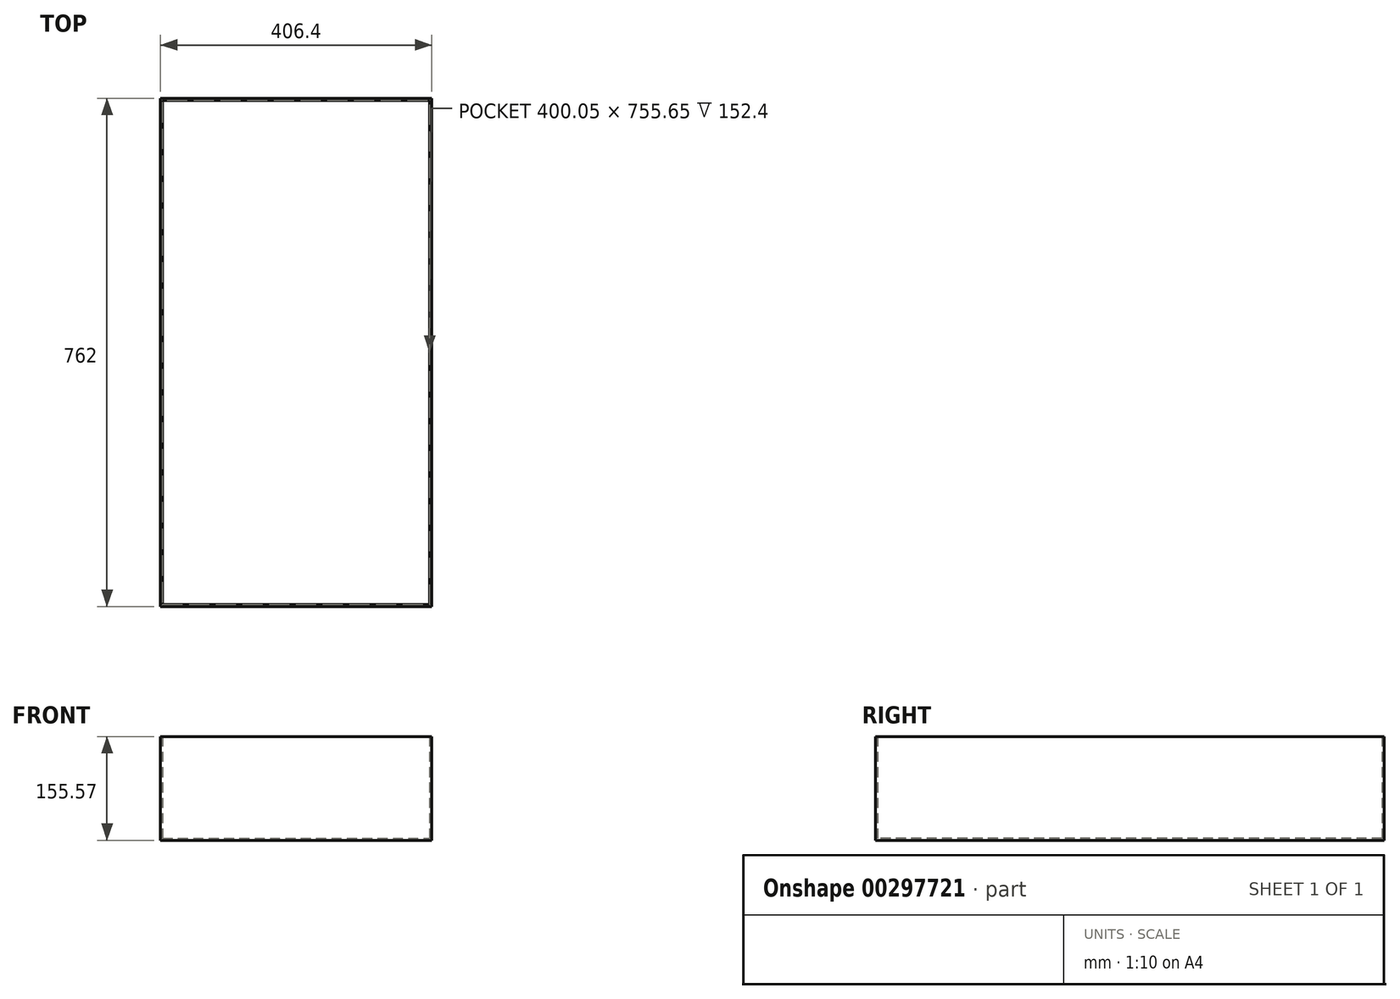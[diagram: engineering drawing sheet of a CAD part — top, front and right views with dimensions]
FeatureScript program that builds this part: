
annotation { "Feature Type Name" : "Feature", "Feature Type Description" : "" }
export const myFeature = defineFeature(function(context is Context, id is Id, definition is map)
    precondition{}
    {
        {
            var Q0;
            Q0=qCreatedBy(makeId("Top.planeOp"),FACE);
            var sketch = newSketch(context, id + "F0", { "sketchPlane" : qUnion([Q0])});
            skLineSegment(sketch, "E0.bottom", {"start": v(203.2, 381) * mm, "end": v(-203.2, 381) * mm});
            skLineSegment(sketch, "E0.top", {"start": v(203.2, -381) * mm, "end": v(-203.2, -381) * mm});
            skLineSegment(sketch, "E0.left", {"start": v(203.2, 381) * mm, "end": v(203.2, -381) * mm});
            skLineSegment(sketch, "E0.right", {"start": v(-203.2, 381) * mm, "end": v(-203.2, -381) * mm});
            skPoint(sketch, "E0.middle", {"position": v(0, 0) * mm});
            skSolve(sketch);
        }
        {
            var Q0;
            Q0 = qSketchRegion(id + "F0", true);
            extrude(context, id + "F1", {"entities" : qUnion([Q0]), "depth" : 3.17 * mm});
        }
        {
            var Q0;
            Q0=makeQuery(id+"F1.opExtrude","CAP_FACE",FACE,{"disambiguationData":[OSD([sQuery(id+"F0.wireOp",EDGE,"E0.bottom"),sQuery(id+"F0.wireOp",EDGE,"E0.top"),sQuery(id+"F0.wireOp",EDGE,"E0.left"),sQuery(id+"F0.wireOp",EDGE,"E0.right")])],"isStart":false});
            var sketch = newSketch(context, id + "F2", { "sketchPlane" : qUnion([Q0])});
            skPoint(sketch, "E1.0", {"position": v(-203.2, 381) * mm});
            skLineSegment(sketch, "E2", {"start": v(-203.2, 381) * mm, "end": v(-203.2, 377.83) * mm});
            skLineSegment(sketch, "E3", {"start": v(-203.2, 377.83) * mm, "end": v(203.2, 377.83) * mm});
            skLineSegment(sketch, "E4", {"start": v(203.2, 377.83) * mm, "end": v(203.2, 381) * mm});
            skLineSegment(sketch, "E5", {"start": v(203.2, 381) * mm, "end": v(-203.2, 381) * mm});
            skSolve(sketch);
        }
        {
            var Q0;
            Q0 = qSketchRegion(id + "F2", true);
            extrude(context, id + "F3", {"entities" : qUnion([Q0]), "operationType" : NewBodyOperationType.ADD, "depth" : 152.4 * mm});
        }
        {
            var Q0;
            Q0=makeQuery(id+"F1.opExtrude","CAP_FACE",FACE,{"disambiguationData":[OSD([sQuery(id+"F0.wireOp",EDGE,"E0.bottom"),sQuery(id+"F0.wireOp",EDGE,"E0.top"),sQuery(id+"F0.wireOp",EDGE,"E0.left"),sQuery(id+"F0.wireOp",EDGE,"E0.right")])],"isStart":false});
            var sketch = newSketch(context, id + "F4", { "sketchPlane" : qUnion([Q0])});
            skPoint(sketch, "E6.0", {"position": v(203.2, 377.83) * mm});
            skLineSegment(sketch, "E7", {"start": v(203.2, 377.83) * mm, "end": v(200.02, 377.83) * mm});
            skLineSegment(sketch, "E8", {"start": v(200.02, 377.83) * mm, "end": v(200.02, -381) * mm});
            skLineSegment(sketch, "E9", {"start": v(200.02, -381) * mm, "end": v(203.2, -381) * mm});
            skLineSegment(sketch, "E10", {"start": v(203.2, -381) * mm, "end": v(203.2, 377.83) * mm});
            skSolve(sketch);
        }
        {
            var Q0;
            Q0 = qSketchRegion(id + "F4", true);
            extrude(context, id + "F5", {"entities" : qUnion([Q0]), "operationType" : NewBodyOperationType.ADD, "depth" : 152.4 * mm});
        }
        {
            var Q0;
            Q0=makeQuery(id+"F1.opExtrude","CAP_FACE",FACE,{"disambiguationData":[OSD([sQuery(id+"F0.wireOp",EDGE,"E0.bottom"),sQuery(id+"F0.wireOp",EDGE,"E0.top"),sQuery(id+"F0.wireOp",EDGE,"E0.left"),sQuery(id+"F0.wireOp",EDGE,"E0.right")])],"isStart":false});
            var sketch = newSketch(context, id + "F6", { "sketchPlane" : qUnion([Q0])});
            skPoint(sketch, "E11.0", {"position": v(200.03, -381) * mm});
            skLineSegment(sketch, "E12", {"start": v(200.02, -381) * mm, "end": v(200.02, -377.83) * mm});
            skLineSegment(sketch, "E13", {"start": v(200.02, -377.83) * mm, "end": v(-203.2, -377.83) * mm});
            skLineSegment(sketch, "E14", {"start": v(-203.2, -377.83) * mm, "end": v(-203.2, -381) * mm});
            skLineSegment(sketch, "E15", {"start": v(-203.2, -381) * mm, "end": v(200.02, -381) * mm});
            skSolve(sketch);
        }
        {
            var Q0;
            Q0 = qSketchRegion(id + "F6", true);
            extrude(context, id + "F7", {"entities" : qUnion([Q0]), "operationType" : NewBodyOperationType.ADD, "depth" : 152.4 * mm});
        }
        {
            var Q0;
            Q0=makeQuery(id+"F1.opExtrude","CAP_FACE",FACE,{"disambiguationData":[OSD([sQuery(id+"F0.wireOp",EDGE,"E0.bottom"),sQuery(id+"F0.wireOp",EDGE,"E0.top"),sQuery(id+"F0.wireOp",EDGE,"E0.left"),sQuery(id+"F0.wireOp",EDGE,"E0.right")])],"isStart":false});
            var sketch = newSketch(context, id + "F8", { "sketchPlane" : qUnion([Q0])});
            skPoint(sketch, "E16.0", {"position": v(-203.2, 377.83) * mm});
            skLineSegment(sketch, "E17", {"start": v(-203.2, 377.83) * mm, "end": v(-200.03, 377.83) * mm});
            skLineSegment(sketch, "E18", {"start": v(-200.03, 377.83) * mm, "end": v(-200.03, -377.83) * mm});
            skLineSegment(sketch, "E19", {"start": v(-200.02, -377.83) * mm, "end": v(-203.2, -377.83) * mm});
            skLineSegment(sketch, "E20", {"start": v(-203.2, -377.83) * mm, "end": v(-203.2, 377.83) * mm});
            skSolve(sketch);
        }
        {
            var Q0;
            Q0 = qSketchRegion(id + "F8", true);
            extrude(context, id + "F9", {"entities" : qUnion([Q0]), "operationType" : NewBodyOperationType.ADD, "depth" : 152.4 * mm});
        }
    });
